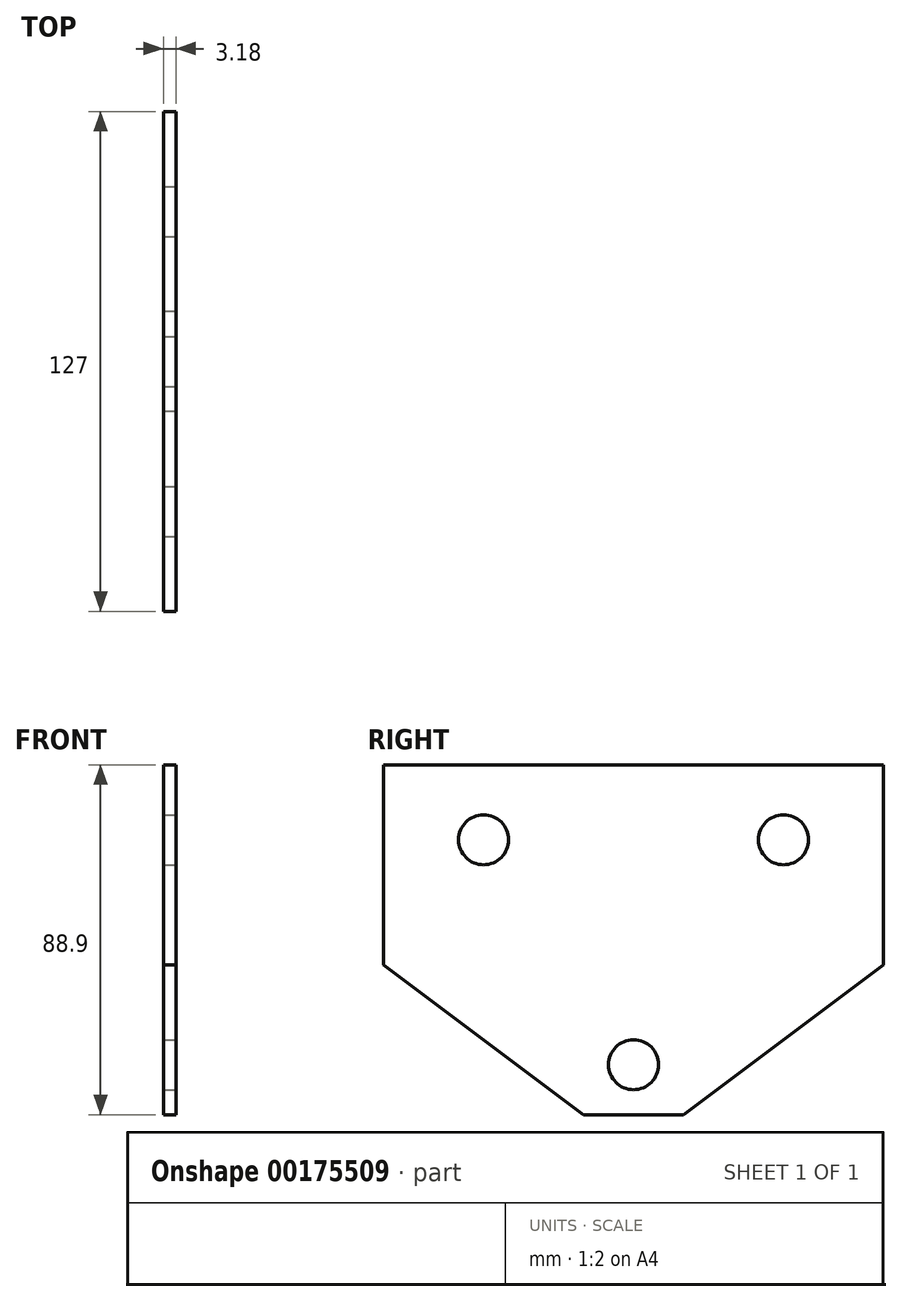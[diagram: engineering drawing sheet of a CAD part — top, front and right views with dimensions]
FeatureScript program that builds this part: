
annotation { "Feature Type Name" : "Feature", "Feature Type Description" : "" }
export const myFeature = defineFeature(function(context is Context, id is Id, definition is map)
    precondition{}
    {
        {
            var Q0;
            Q0=qCreatedBy(makeId("Right.planeOp"),FACE);
            var sketch = newSketch(context, id + "F0", { "sketchPlane" : qUnion([Q0])});
            skLineSegment(sketch, "E0", {"start": v(-63.5, 38.1) * mm, "end": v(63.5, 38.1) * mm});
            skLineSegment(sketch, "E1", {"start": v(63.5, 38.1) * mm, "end": v(63.5, -12.7) * mm});
            skLineSegment(sketch, "E2", {"start": v(63.5, -12.7) * mm, "end": v(12.7, -50.8) * mm});
            skLineSegment(sketch, "E3", {"start": v(12.7, -50.8) * mm, "end": v(-12.7, -50.8) * mm});
            skLineSegment(sketch, "E4", {"start": v(-12.7, -50.8) * mm, "end": v(-63.5, -12.7) * mm});
            skLineSegment(sketch, "E5", {"start": v(-63.5, -12.7) * mm, "end": v(-63.5, 38.1) * mm});
            skSolve(sketch);
        }
        {
            var Q0;
            Q0=makeQuery(id+"F0.imprint","IMPRINT",FACE,{"disambiguationData":[TD([[makeQuery(id+"F0.imprint","IMPRINT",EDGE,{"derivedFrom":sQuery(id+"F0.wireOp",EDGE,"E0")}),-1.0]])]});
            extrude(context, id + "F1", {"entities" : qUnion([Q0]), "depth" : 3.17 * mm});
        }
        {
            var Q0;
            Q0=makeQuery(id+"F1.opExtrude","CAP_FACE",FACE,{"disambiguationData":[OSD([sQuery(id+"F0.wireOp",EDGE,"E0"),sQuery(id+"F0.wireOp",EDGE,"E1"),sQuery(id+"F0.wireOp",EDGE,"E2"),sQuery(id+"F0.wireOp",EDGE,"E3"),sQuery(id+"F0.wireOp",EDGE,"E4"),sQuery(id+"F0.wireOp",EDGE,"E5")])],"isStart":false});
            var sketch = newSketch(context, id + "F2", { "sketchPlane" : qUnion([Q0])});
            skCircle(sketch, "E6", {"center": v(-38.1, 19.05) * mm, "radius": 6.35 * mm});
            skCircle(sketch, "E7", {"center": v(38.1, 19.05) * mm, "radius": 6.35 * mm});
            skCircle(sketch, "E8", {"center": v(0, -38.1) * mm, "radius": 6.35 * mm});
            skSolve(sketch);
        }
        {
            var Q0;
            Q0=makeQuery(id+"F2.imprint","IMPRINT",FACE,{"disambiguationData":[TD([[makeQuery(id+"F2.imprint","IMPRINT",EDGE,{"derivedFrom":sQuery(id+"F2.wireOp",EDGE,"E6")}),1.0]])]});
            var Q1;
            Q1=makeQuery(id+"F2.imprint","IMPRINT",FACE,{"disambiguationData":[TD([[makeQuery(id+"F2.imprint","IMPRINT",EDGE,{"derivedFrom":sQuery(id+"F2.wireOp",EDGE,"E7")}),1.0]])]});
            var Q2;
            Q2=makeQuery(id+"F2.imprint","IMPRINT",FACE,{"disambiguationData":[TD([[makeQuery(id+"F2.imprint","IMPRINT",EDGE,{"derivedFrom":sQuery(id+"F2.wireOp",EDGE,"E8")}),1.0]])]});
            extrude(context, id + "F3", {"entities" : qUnion([Q0, Q1, Q2]), "operationType" : NewBodyOperationType.REMOVE, "endBound" : BoundingType.UP_TO_NEXT, "oppositeDirection" : true, "depth" : 25.4 * mm});
        }
    });
